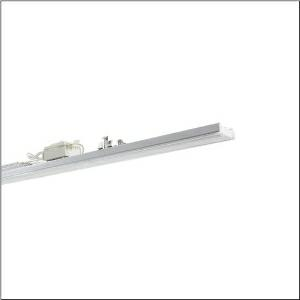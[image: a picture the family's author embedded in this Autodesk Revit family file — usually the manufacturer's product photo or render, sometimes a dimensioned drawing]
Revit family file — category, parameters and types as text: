
# Revit family: licross_11_recessed_ho_51tl12dn455m
name_source: partatom
category: Lighting Fixtures
units: mm (PartAtom-declared; Revit-internal decimal feet)

## family parameters
Cut with Voids When Loaded = No
Host = Face
Light Source = No
Part Type = Normal
Room Calculation Point = No
Round Connector Dimension = Use Diameter
Shared = No

## types (1)
- --- (1 x LED, 5960 lm, 30.6 W, 4000K)
    Apparent Load = 31 VA
    CIE Flux Codes = 66 91 98 100 100
    Color Rendering = 80
    Color Temperature = 4000K
    Default Elevation = 1800 mm
    Description = Licross 11 Recessed HO, luminaire insert, of sheet steel, coil coated, white, length: 1.500mm, width: 66mm, height: 67mm, LED rated luminous flux: 5.960lm, light colour: 840, SDCM (Standard Deviation of Colour Matching)MacAdam ≤ 2 SDCM (initial), control gear: DALI 2, with plug, 5-pole, with phase selection, mains connection: 220..240V, AC, 50/60Hz, rated input power: 31W, internal wiring halogen-free, primary optical cover: cover, of PMMA, light emission: direct distribution, primary light characteristic: symmetric, protection rating (complete): IP40, insulation class (complete): insulation class I (protective earthing), certification: CE, ENEC, VDE, UKCA, protection symbol: D if used in an environment without relevant dust loads with corresponding accessories, impact resistance: IK06, permissible ambient temperature for indoor applications: -25..+45°C, corresponds to IFS (International Featured Standards) requirements for safety and quality in the food industry, reducing of maximum allowable ambient temperature of 5°C with ceiling mounting, LABS conformity tested according to VDMA 24364:2018-05, The light source and the operating device comply with the requirements of the Ecodesign Regulation (EU) 2019/2020 and are replaceable in accordance with this regulation, packaging unit: 1 piece
    Height = 58 mm
    Lamp = 1 x LED
    Lamp Light Flux = 5960 lm
    Lamp Power = 30.6 W
    Lamp count = 1
    Length = 1500 mm
    Luminous efficacy = 195 lm/W
    Manufacturer = Siteco
    ModVariant = No
    Model = 51TL12DN455M
    Mounting Place = Ceiling
    Mounting Type = Pendant
    Number of Poles = 1
    OnlyDefault = Yes
    Power Factor = 1
    Product Name = Licross 11 Recessed HO
    Product group = luminaire insert | ceiling pendant
    ProductGroupID = 901
    Protection Class = Protection class I
    Protection Degree = IP 40
    RLX_Detail_Level = 1
    RLX_Emergency_Light_Flux = 0 lm
    RLX_Emergency_Type = 0
    RLX_Emergency_Type_DB = No
    RlxData = <blob elided: 24573 chars, md5=f44d1b44>
    Socket = socket
    Standby Power = 0 W
    System Light Flux = 5960 lm
    System Power = 31 W
    Type Comments = factory setting: luminous flux: 100 % | dim-lin: 254 | 212 mA
    Type Image = l_1296930.jpg
    URL = http://relux.com
    VarID = @adj_101151
    Voltage = 0 V
    Weight = 0.00 kg
    Width = 66 mm

## geometry (parser evidence)
native form markers: Blend x4, Sweep x9
no freeform markers — native parametric forms only
